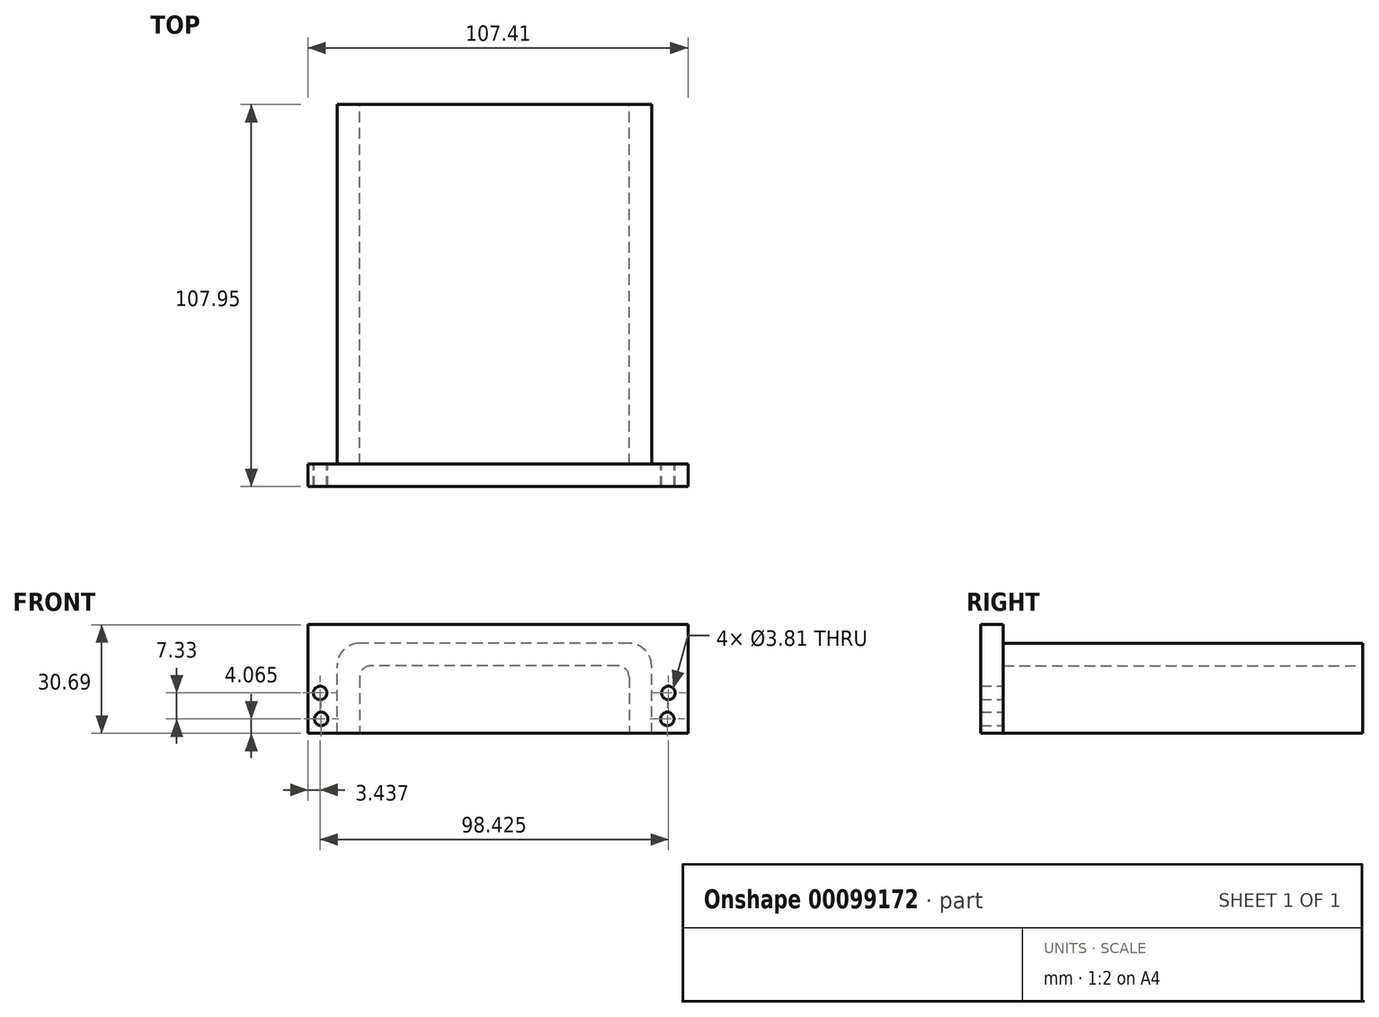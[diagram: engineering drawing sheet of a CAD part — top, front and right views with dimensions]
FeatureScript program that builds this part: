
annotation { "Feature Type Name" : "Feature", "Feature Type Description" : "" }
export const myFeature = defineFeature(function(context is Context, id is Id, definition is map)
    precondition{}
    {
        {
            var Q0;
            Q0=qCreatedBy(makeId("Front.planeOp"),FACE);
            var sketch = newSketch(context, id + "F0", { "sketchPlane" : qUnion([Q0])});
            skLineSegment(sketch, "E0", {"start": v(0, 19.05) * mm, "end": v(-34.92, 19.05) * mm});
            skLineSegment(sketch, "E1", {"start": v(-38.1, 15.88) * mm, "end": v(-38.1, 0) * mm});
            skLineSegment(sketch, "E2", {"start": v(-38.1, 0) * mm, "end": v(-44.45, 0) * mm});
            skLineSegment(sketch, "E3", {"start": v(-44.45, 0) * mm, "end": v(-44.45, 19.05) * mm});
            skPoint(sketch, "E4.start.orphan", {"position": v(25.92, 0) * mm});
            skLineSegment(sketch, "E5", {"start": v(-38.1, 25.4) * mm, "end": v(0, 25.4) * mm});
            skLineSegment(sketch, "E6.MirrorCS", {"start": v(38.1, 15.88) * mm, "end": v(38.1, 0) * mm});
            skLineSegment(sketch, "E7.MirrorCS", {"start": v(38.1, 0) * mm, "end": v(44.45, 0) * mm});
            skLineSegment(sketch, "E8.MirrorCS", {"start": v(44.45, 0) * mm, "end": v(44.45, 19.05) * mm});
            skLineSegment(sketch, "E9.MirrorCS", {"start": v(0, 19.05) * mm, "end": v(34.92, 19.05) * mm});
            skLineSegment(sketch, "E10.MirrorCS", {"start": v(38.1, 25.4) * mm, "end": v(0, 25.4) * mm});
            skPoint(sketch, "E11.visualSharp", {"position": v(-44.45, 25.4) * mm});
            skArc(sketch, "E11.filletArc", {"start": v(-38.1, 25.4) * mm, "mid": v(-42.6, 23.54) * mm, "end": v(-44.45, 19.05) * mm});
            skPoint(sketch, "E12.visualSharp", {"position": v(44.45, 25.4) * mm});
            skArc(sketch, "E12.filletArc", {"start": v(44.45, 19.05) * mm, "mid": v(42.6, 23.54) * mm, "end": v(38.1, 25.4) * mm});
            skArc(sketch, "E13.filletArc", {"start": v(38.1, 15.88) * mm, "mid": v(37.17, 18.12) * mm, "end": v(34.92, 19.05) * mm});
            skArc(sketch, "E14.filletArc", {"start": v(-34.92, 19.05) * mm, "mid": v(-37.17, 18.12) * mm, "end": v(-38.1, 15.88) * mm});
            skSolve(sketch);
        }
        {
            var Q0;
            Q0=makeQuery(id+"F0.imprint","IMPRINT",FACE,{"disambiguationData":[TD([[makeQuery(id+"F0.imprint","IMPRINT",EDGE,{"derivedFrom":sQuery(id+"F0.wireOp",EDGE,"E0")}),-1.0]])]});
            extrude(context, id + "F1", {"entities" : qUnion([Q0]), "depth" : 101.6 * mm});
        }
        {
            var Q0;
            Q0=makeQuery(id+"F1.opExtrude","CAP_FACE",FACE,{"disambiguationData":[OSD([sQuery(id+"F0.wireOp",EDGE,"E0"),sQuery(id+"F0.wireOp",EDGE,"E1"),sQuery(id+"F0.wireOp",EDGE,"E2"),sQuery(id+"F0.wireOp",EDGE,"E3"),sQuery(id+"F0.wireOp",EDGE,"E5"),sQuery(id+"F0.wireOp",EDGE,"E6.MirrorCS"),sQuery(id+"F0.wireOp",EDGE,"E7.MirrorCS"),sQuery(id+"F0.wireOp",EDGE,"E8.MirrorCS"),sQuery(id+"F0.wireOp",EDGE,"E9.MirrorCS"),sQuery(id+"F0.wireOp",EDGE,"E10.MirrorCS"),sQuery(id+"F0.wireOp",EDGE,"E11.filletArc"),sQuery(id+"F0.wireOp",EDGE,"E12.filletArc"),sQuery(id+"F0.wireOp",EDGE,"E13.filletArc"),sQuery(id+"F0.wireOp",EDGE,"E14.filletArc")])],"isStart":false});
            var sketch = newSketch(context, id + "F2", { "sketchPlane" : qUnion([Q0])});
            skLineSegment(sketch, "E15", {"start": v(0, 0) * mm, "end": v(-52.65, 0) * mm});
            skLineSegment(sketch, "E16", {"start": v(-52.65, 0) * mm, "end": v(-52.65, 30.7) * mm});
            skLineSegment(sketch, "E17", {"start": v(-52.65, 30.7) * mm, "end": v(54.76, 30.7) * mm});
            skLineSegment(sketch, "E18", {"start": v(54.76, 30.7) * mm, "end": v(54.76, 0) * mm});
            skLineSegment(sketch, "E19", {"start": v(54.76, 0) * mm, "end": v(0, 0) * mm});
            skCircle(sketch, "E20", {"center": v(-48.91, 4.07) * mm, "radius": 1.9 * mm});
            skCircle(sketch, "E21", {"center": v(-49.21, 11.4) * mm, "radius": 1.9 * mm});
            skCircle(sketch, "E22.MirrorC", {"center": v(49.21, 11.4) * mm, "radius": 1.9 * mm});
            skCircle(sketch, "E23.MirrorC", {"center": v(48.91, 4.07) * mm, "radius": 1.9 * mm});
            skSolve(sketch);
        }
        {
            var Q0;
            {var subQ5=sQuery(id+"F2.wireOp",EDGE,"E16");Q0=makeQuery(id+"F2.imprint","IMPRINT",FACE,{"disambiguationData":[TD([[makeQuery(id+"F2.imprint","IMPRINT",EDGE,{"derivedFrom":subQ5}),-1.0]])]});}
            var Q1;
            {var subQ0=makeQuery(id+"F1.opExtrude","CAP_EDGE",EDGE,{"disambiguationData":[OSD([sQuery(id+"F0.wireOp",EDGE,"E1")])],"isStart":false});Q1=makeQuery(id+"F2.imprint","IMPRINT",FACE,{"disambiguationData":[TD([[makeQuery(id+"F2.imprint","IMPRINT",EDGE,{"derivedFrom":subQ0}),1.0]])]});}
            var Q2;
            {var subQ5=makeQuery(id+"F1.opExtrude","CAP_EDGE",EDGE,{"disambiguationData":[OSD([sQuery(id+"F0.wireOp",EDGE,"E1")])],"isStart":false});Q2=makeQuery(id+"F2.imprint","IMPRINT",FACE,{"disambiguationData":[TD([[makeQuery(id+"F2.imprint","IMPRINT",EDGE,{"derivedFrom":subQ5}),-1.0]])]});}
            extrude(context, id + "F3", {"entities" : qUnion([Q0, Q1, Q2]), "operationType" : NewBodyOperationType.ADD, "depth" : 6.35 * mm});
        }
    });
